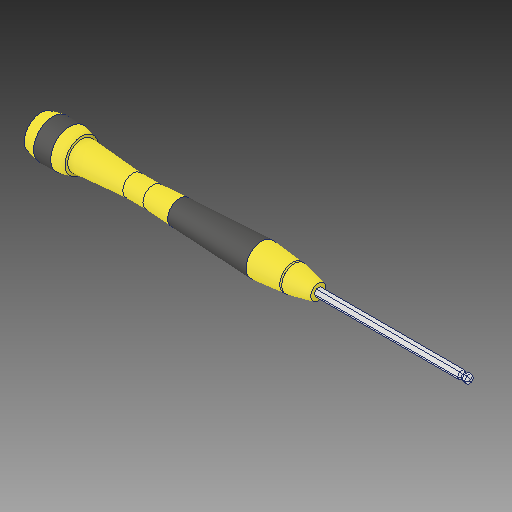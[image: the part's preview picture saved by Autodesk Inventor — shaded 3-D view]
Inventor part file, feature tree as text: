
AUTODESK INVENTOR PART (.ipt)
format: ipt  version: 2018 (Build 220112000, 112)  size: 161,792 bytes
history: native  units: in
note: dims shown in document units (in); Inventor stores cm internally (conversion verified against a paired STEP export)
features: fillet x1
ambient origin geometry x8: Origin, YZ Plane, XZ Plane, XY Plane, X Axis, Y Axis, Z Axis, Center Point
bodies: Solid1 (feature_tree)
feature tree (1):
  fillet  "Fillet1"  [1 undecoded]
note: 1 required parameter value undecoded (feature->parameter linkage not recoverable at this tier; creation-order binding heuristic only, values carry confidence <= 0.55)
